# Revit family: Electronics_Touch-Panels_Biamp_Apprimo_TEC-X-Networked-AV-Control-Pad__
name_source: partatom
category: Communication Devices
units: mm (PartAtom-declared; Revit-internal decimal feet)

## family parameters
Cut with Voids When Loaded = No
Host = Face
Maintain Annotation Orientation = No
OmniClass Number = 23.85.10.17.11
OmniClass Title = Audio-Visual System Components
Part Type = Normal
Room Calculation Point = No
Round Connector Dimension = Use Diameter
Shared = No

## types (4) — shared parameters
Altitude = 0-10,000 ft (0-3000m) MSL
Apparent Load = 2 VA
Apprimo TEC-X 1000 = Apprimo TEC-X 1000
Apprimo TEC-X 2000 = Apprimo TEC-X 2000
Compliance = FCC Part 15B (USA) CE marked (Europe) UL and C-UL listed (USA and Canada) RoHS Directive (Europe)
Connector Description = PoE (IEEE 802.3at Class 3, 15W)
Daisy Chain Length = 4 devices max
Default Elevation = 48 "
Depth = 0.5 "
Display Type = High-Contrast Capacitive Touch LCD
Height = 5.1 "
Humidity = 0-95% relative humidity (non-condensing)
Manufacturer = Biamp
Max Power Consumption = 2 W
Network Connection = RJ-45 with Ethernet cable (Cat 5e and above)
Number of Poles = 1
Power Factor = 1
Product Documentation Link = https://downloads.biamp.com
Product Page URL = https://www.biamp.com
Product data url = https://www.bimobject.com
Status Indicator = RGB LED bar with adjustable brightness
Temperature Range = 32 - 104° F (0 - 40° C)
URL = https://www.biamp.com
Voltage = 0 V
Width = 3.5 "

## per-type parameters (varying)
| type | Description | Display Size | Housing Material | Model | Model name | Weight |
| TEC-X 1000 White | Apprimo TEC-X 1000 Networked AV Control Pad with Rotary Knob | 2.9 " | Biamp - Plastic - White | Apprimo TEC-X 1000 | Apprimo TEC-X 1000 | 0.35 lb |
| TEC-X 2000 White | Apprimo TEC-X 2000 Networked AV Control Pad | 3.8 " | Biamp - Plastic - White | Apprimo TEC-X 2000 | Apprimo TEC-X 2000 | 0.30 lb |
| TEC-X 1000 Black | Apprimo TEC-X 1000 Networked AV Control Pad with Rotary Knob | 2.9 " | Biamp - Plastic - Black | Apprimo TEC-X 1000 | Apprimo TEC-X 1000 | 0.35 lb |
| TEC-X 2000 Black | Apprimo TEC-X 2000 Networked AV Control Pad | 3.8 " | Biamp - Plastic - Black | Apprimo TEC-X 2000 | Apprimo TEC-X 2000 | 0.30 lb |

## geometry (parser evidence)
native form markers: Sweep x11
no freeform markers — native parametric forms only
